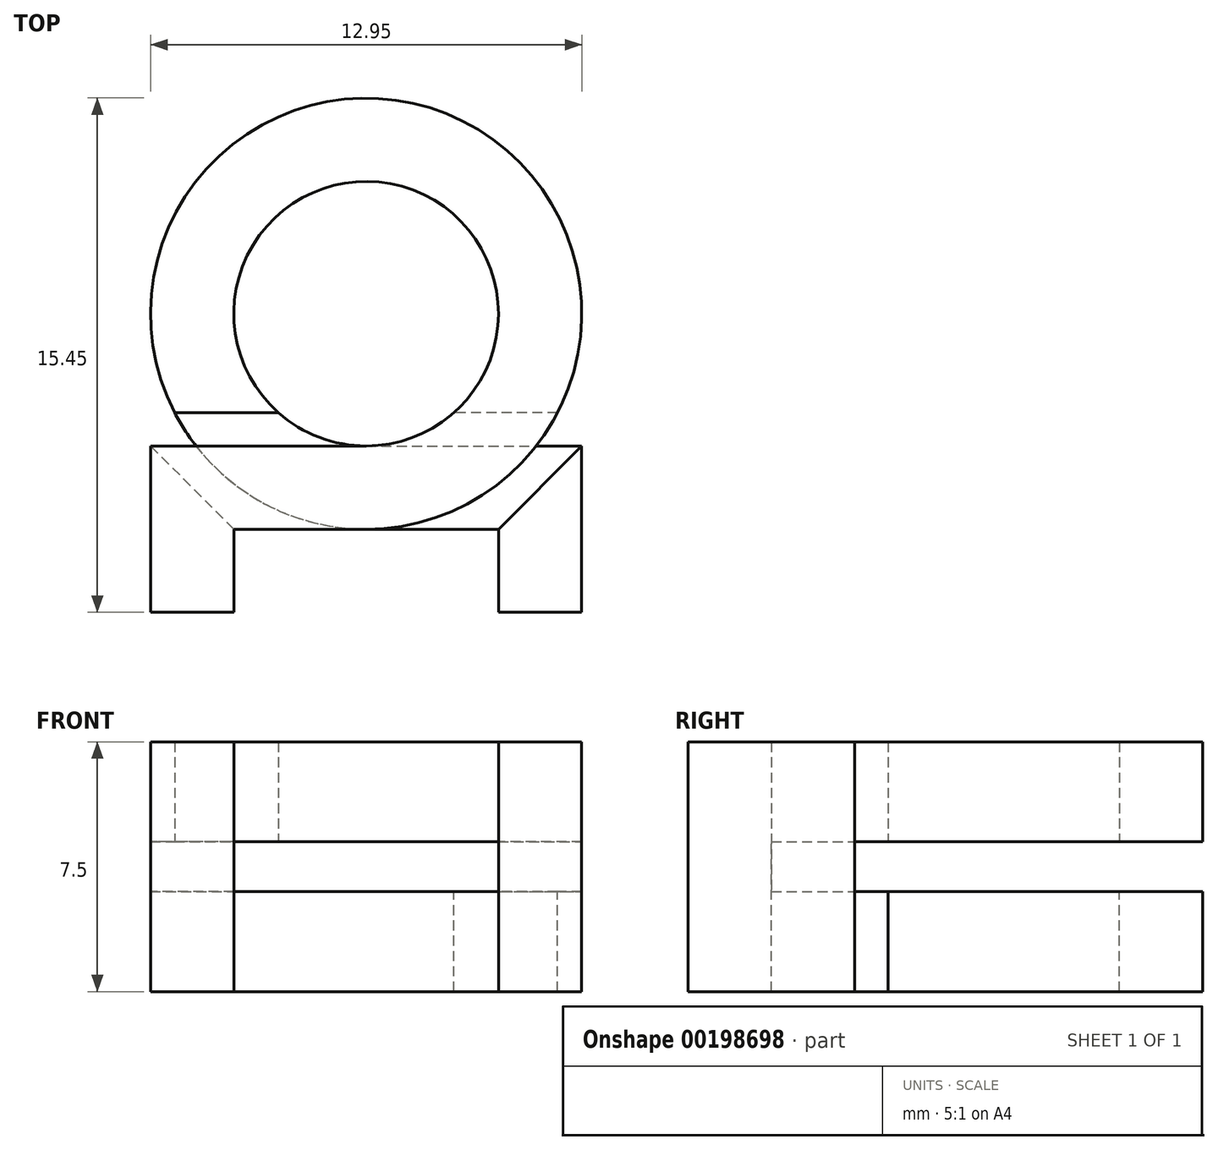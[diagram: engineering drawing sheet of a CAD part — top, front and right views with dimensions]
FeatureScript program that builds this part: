
annotation { "Feature Type Name" : "Feature", "Feature Type Description" : "" }
export const myFeature = defineFeature(function(context is Context, id is Id, definition is map)
    precondition{}
    {
        {
            var Q0;
            Q0=qCreatedBy(makeId("Top.planeOp"),FACE);
            var sketch = newSketch(context, id + "F4", { "sketchPlane" : qUnion([Q0])});
            skCircle(sketch, "E0", {"center": v(0, 0) * mm, "radius": 3.98 * mm, "construction": true});
            skCircle(sketch, "E1.0", {"center": v(0, 0) * mm, "radius": 6.47 * mm, "construction": true});
            skLineSegment(sketch, "E2", {"start": v(0, -3.97) * mm, "end": v(-6.47, -3.98) * mm});
            skLineSegment(sketch, "E3", {"start": v(0, -6.47) * mm, "end": v(-3.97, -6.47) * mm});
            skLineSegment(sketch, "E4", {"start": v(-6.47, -3.98) * mm, "end": v(-6.47, -8.97) * mm});
            skLineSegment(sketch, "E5", {"start": v(-6.47, -8.98) * mm, "end": v(-3.97, -8.98) * mm});
            skLineSegment(sketch, "E6", {"start": v(-3.97, -8.97) * mm, "end": v(-3.97, -6.48) * mm});
            skLineSegment(sketch, "E7", {"start": v(-5.75, -2.98) * mm, "end": v(-2.64, -2.98) * mm});
            skArc(sketch, "E8", {"start": v(-2.64, -2.98) * mm, "mid": v(1.4, 3.72) * mm, "end": v(0, -3.98) * mm});
            skArc(sketch, "E9", {"start": v(-5.75, -2.98) * mm, "mid": v(3.37, 5.53) * mm, "end": v(0, -6.47) * mm});
            skLineSegment(sketch, "E10", {"start": v(0, 0) * mm, "end": v(0, 17.54) * mm});
            skLineSegment(sketch, "E11", {"start": v(2.64, -2.98) * mm, "end": v(5.75, -2.98) * mm, "construction": true});
            skSolve(sketch);
        }
        {
            var Q0;
            Q0=qSketchRegion(id+"F4",true);
            extrude(context, id + "F5", {"entities" : qUnion([Q0]), "depth" : 3 * mm, "symmetric" : true});
        }
        {
            var Q0;
            Q0=makeQuery(id+"F5.opExtrude","CAP_FACE",FACE,{"disambiguationData":[OSD([sQuery(id+"F4.wireOp",EDGE,"E2"),sQuery(id+"F4.wireOp",EDGE,"E3"),sQuery(id+"F4.wireOp",EDGE,"E4"),sQuery(id+"F4.wireOp",EDGE,"E5"),sQuery(id+"F4.wireOp",EDGE,"E6"),sQuery(id+"F4.wireOp",EDGE,"E7"),sQuery(id+"F4.wireOp",EDGE,"E8"),sQuery(id+"F4.wireOp",EDGE,"E9")])],"isStart":true});
            var sketch = newSketch(context, id + "F0", { "sketchPlane" : qUnion([Q0])});
            skLineSegment(sketch, "E12.0", {"start": v(-6.47, 3.98) * mm, "end": v(-6.47, 8.97) * mm});
            skLineSegment(sketch, "E13.0", {"start": v(-3.97, 8.98) * mm, "end": v(-3.97, 6.48) * mm});
            skLineSegment(sketch, "E14.0", {"start": v(-6.47, 8.98) * mm, "end": v(-3.97, 8.98) * mm});
            skLineSegment(sketch, "E15", {"start": v(-3.97, 6.48) * mm, "end": v(-6.47, 3.98) * mm});
            skSolve(sketch);
        }
        {
            var Q0;
            Q0=makeQuery(id+"F0.imprint","IMPRINT",FACE,{"disambiguationData":[TD([[makeQuery(id+"F0.imprint","IMPRINT",EDGE,{"derivedFrom":sQuery(id+"F0.wireOp",EDGE,"E12.0")}),1.0]])]});
            var Q1;
            Q1=qSketchRegion(id+"F0",true);
            extrude(context, id + "F1", {"entities" : qUnion([Q0, Q1]), "operationType" : NewBodyOperationType.ADD, "depth" : 4.5 * mm});
        }
        {
            var Q0;
            Q0=makeQuery(id+"F5.opExtrude","SWEPT_BODY",BODY,{"disambiguationData":[OSD([sQuery(id+"F4.wireOp",EDGE,"E2"),sQuery(id+"F4.wireOp",EDGE,"E3"),sQuery(id+"F4.wireOp",EDGE,"E4"),sQuery(id+"F4.wireOp",EDGE,"E5"),sQuery(id+"F4.wireOp",EDGE,"E6"),sQuery(id+"F4.wireOp",EDGE,"E7"),sQuery(id+"F4.wireOp",EDGE,"E8"),sQuery(id+"F4.wireOp",EDGE,"E9")])]});
            transform(context, id + "F2", {"entities" : qUnion([Q0]), "transformType" : TransformType.TRANSLATION_3D, "dx" : 0 * mm, "dy" : 0 * mm, "dz" : 4.5 * mm, "makeCopy" : true});
        }
        {
            var Q0;
            Q0=makeQuery(id+"F5.opExtrude","SWEPT_BODY",BODY,{"disambiguationData":[OSD([sQuery(id+"F4.wireOp",EDGE,"E2"),sQuery(id+"F4.wireOp",EDGE,"E3"),sQuery(id+"F4.wireOp",EDGE,"E4"),sQuery(id+"F4.wireOp",EDGE,"E5"),sQuery(id+"F4.wireOp",EDGE,"E6"),sQuery(id+"F4.wireOp",EDGE,"E7"),sQuery(id+"F4.wireOp",EDGE,"E8"),sQuery(id+"F4.wireOp",EDGE,"E9")])]});
            var Q1;
            Q1=sQuery(id+"F4.wireOp",EDGE,"E10");
            transform(context, id + "F3", {"entities" : qUnion([Q0]), "transformType" : TransformType.ROTATION, "transformAxis" : qUnion([Q1]), "angle" : 180 * degree, "makeCopy" : false});
        }
    });
